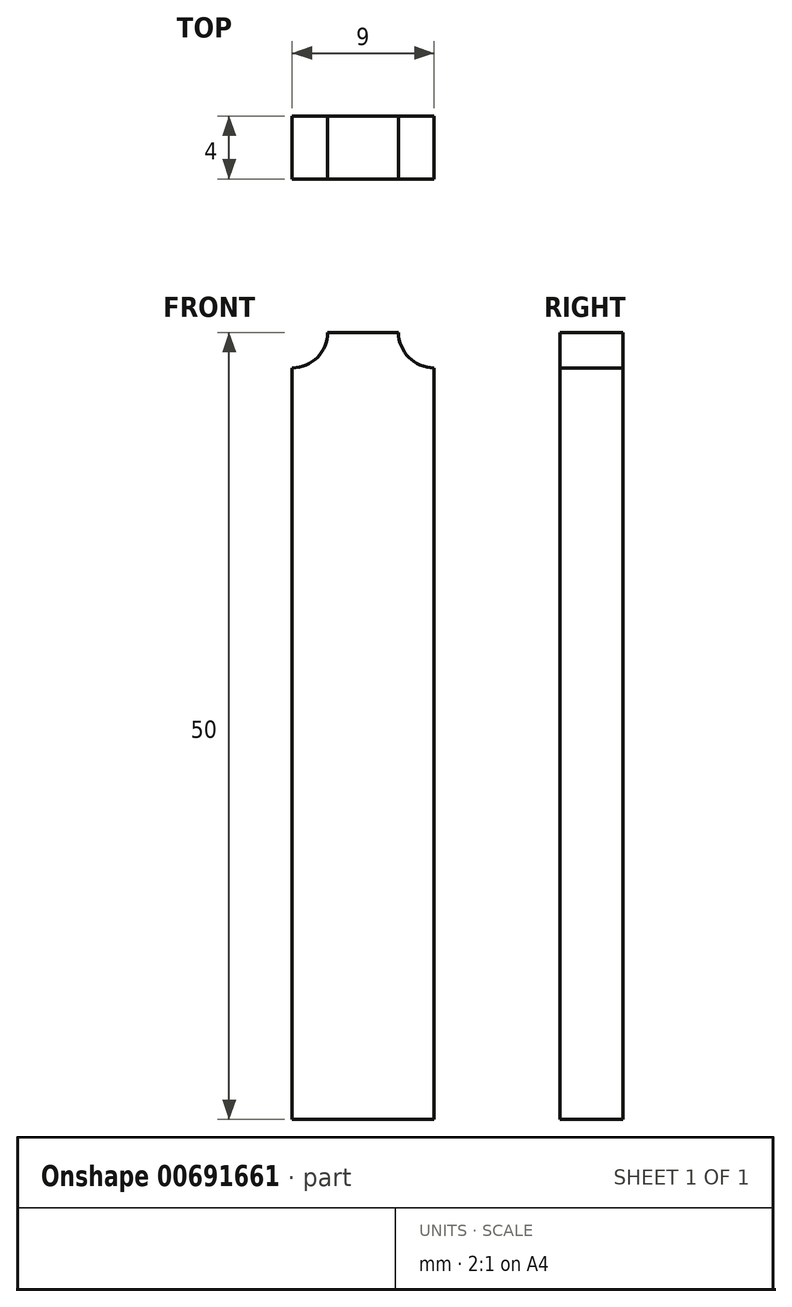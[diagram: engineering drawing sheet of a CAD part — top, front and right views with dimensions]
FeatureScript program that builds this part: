
annotation { "Feature Type Name" : "Feature", "Feature Type Description" : "" }
export const myFeature = defineFeature(function(context is Context, id is Id, definition is map)
    precondition{}
    {
        {
            var Q0;
            Q0=qCreatedBy(makeId("Front.planeOp"),FACE);
            var sketch = newSketch(context, id + "F0", { "sketchPlane" : qUnion([Q0])});
            skLineSegment(sketch, "E0.bottom", {"start": v(-4.5, 0) * mm, "end": v(4.5, 0) * mm});
            skLineSegment(sketch, "E0.top", {"start": v(-4.5, -50) * mm, "end": v(4.5, -50) * mm});
            skLineSegment(sketch, "E0.left", {"start": v(-4.5, 0) * mm, "end": v(-4.5, -50) * mm});
            skLineSegment(sketch, "E0.right", {"start": v(4.5, 0) * mm, "end": v(4.5, -50) * mm});
            skLineSegment(sketch, "E1.bottom", {"start": v(-2.25, 29.05) * mm, "end": v(2.25, 29.05) * mm});
            skLineSegment(sketch, "E1.top", {"start": v(-2.25, 0) * mm, "end": v(2.25, 0) * mm});
            skLineSegment(sketch, "E1.left", {"start": v(-2.25, 29.05) * mm, "end": v(-2.25, 0) * mm});
            skLineSegment(sketch, "E1.right", {"start": v(2.25, 29.05) * mm, "end": v(2.25, 0) * mm});
            skLineSegment(sketch, "E2", {"start": v(0, 22) * mm, "end": v(0, 13) * mm});
            skLineSegment(sketch, "E3.bottom", {"start": v(33.74, -3.72) * mm, "end": v(46.18, -3.72) * mm});
            skLineSegment(sketch, "E3.top", {"start": v(33.74, -42.5) * mm, "end": v(46.18, -42.5) * mm});
            skLineSegment(sketch, "E3.left", {"start": v(33.74, -3.72) * mm, "end": v(33.74, -42.5) * mm});
            skLineSegment(sketch, "E3.right", {"start": v(46.18, -3.72) * mm, "end": v(46.18, -42.5) * mm});
            skLineSegment(sketch, "E4", {"start": v(46.18, -8.55) * mm, "end": v(42.11, -6.2) * mm});
            skLineSegment(sketch, "E5", {"start": v(42.11, -6.2) * mm, "end": v(42.11, -13.68) * mm});
            skLineSegment(sketch, "E6", {"start": v(42.11, -13.68) * mm, "end": v(46.18, -11.33) * mm});
            skLineSegment(sketch, "E7.0.1.0", {"start": v(46.18, -20.55) * mm, "end": v(42.11, -18.2) * mm});
            skLineSegment(sketch, "E7.0.1.1", {"start": v(42.11, -18.2) * mm, "end": v(42.11, -25.68) * mm});
            skLineSegment(sketch, "E7.0.1.2", {"start": v(42.11, -25.68) * mm, "end": v(46.18, -23.33) * mm});
            skLineSegment(sketch, "E7.0.2.0", {"start": v(46.18, -32.55) * mm, "end": v(42.11, -30.2) * mm});
            skLineSegment(sketch, "E7.0.2.1", {"start": v(42.11, -30.2) * mm, "end": v(42.11, -37.68) * mm});
            skLineSegment(sketch, "E7.0.2.2", {"start": v(42.11, -37.68) * mm, "end": v(46.18, -35.33) * mm});
            skLineSegment(sketch, "E7.direction1", {"start": v(42.11, -13.68) * mm, "end": v(67.11, -13.68) * mm, "construction": true});
            skLineSegment(sketch, "E7.direction2", {"start": v(42.11, -13.68) * mm, "end": v(42.11, -25.68) * mm, "construction": true});
            skLineSegment(sketch, "E8.0", {"start": v(41.91, -14.03) * mm, "end": v(46.18, -11.57) * mm});
            skLineSegment(sketch, "E8.1", {"start": v(41.91, -5.86) * mm, "end": v(41.91, -14.03) * mm});
            skLineSegment(sketch, "E8.2", {"start": v(46.18, -8.32) * mm, "end": v(41.91, -5.86) * mm});
            skArc(sketch, "E9.0.startCap", {"start": v(-1, 22) * mm, "mid": v(0, 23) * mm, "end": v(1, 22) * mm});
            skArc(sketch, "E9.0.endCap", {"start": v(1, 13) * mm, "mid": v(0, 12) * mm, "end": v(-1, 13) * mm});
            skLineSegment(sketch, "E9.0.left", {"start": v(1, 22) * mm, "end": v(1, 13) * mm});
            skLineSegment(sketch, "E9.0.right", {"start": v(-1, 22) * mm, "end": v(-1, 13) * mm});
            skFitSpline(sketch, "E10", {"points": [v(0, 29.05) * mm, v(-1.01, 28.43) * mm, v(-1.8, 25.53) * mm, v(-2.25, 21.02) * mm], "startDerivative": vector(-5.04, -1.79) * mm, "endDerivative": vector(-0.93, -10.66) * mm});
            skFitSpline(sketch, "E11.MirrorCS", {"points": [v(0, 29.05) * mm, v(1.01, 28.43) * mm, v(1.8, 25.53) * mm, v(2.25, 21.02) * mm], "startDerivative": vector(5.04, -1.79) * mm, "endDerivative": vector(0.93, -10.66) * mm});
            skSolve(sketch);
        }
        {
            var Q0;
            {var subQ1=sQuery(id+"F0.wireOp",EDGE,"E1.top");Q0=makeQuery(id+"F0.imprint","IMPRINT",FACE,{"disambiguationData":[TD([[makeQuery(id+"F0.imprint","IMPRINT",EDGE,{"derivedFrom":subQ1}),1.0]])]});}
            var Q1;
            Q1=makeQuery(id+"F0.imprint","IMPRINT",FACE,{"disambiguationData":[TD([[makeQuery(id+"F0.imprint","IMPRINT",EDGE,{"derivedFrom":sQuery(id+"F0.wireOp",EDGE,"E0.top")}),1.0]])]});
            extrude(context, id + "F1", {"entities" : qUnion([Q0, Q1]), "depth" : 4 * mm, "offsetDistance" : 25 * mm});
        }
        {
            var Q0;
            Q0=makeQuery(id+"F1.opExtrude","CAP_FACE",FACE,{"disambiguationData":[OSD([sQuery(id+"F0.wireOp",EDGE,"E0.bottom"),sQuery(id+"F0.wireOp",EDGE,"E0.top"),sQuery(id+"F0.wireOp",EDGE,"E0.left"),sQuery(id+"F0.wireOp",EDGE,"E0.right"),sQuery(id+"F0.wireOp",EDGE,"E1.left"),sQuery(id+"F0.wireOp",EDGE,"E1.right"),sQuery(id+"F0.wireOp",EDGE,"E9.0.startCap"),sQuery(id+"F0.wireOp",EDGE,"E9.0.endCap"),sQuery(id+"F0.wireOp",EDGE,"E9.0.left"),sQuery(id+"F0.wireOp",EDGE,"E9.0.right"),sQuery(id+"F0.wireOp",EDGE,"E10"),sQuery(id+"F0.wireOp",EDGE,"E11.MirrorCS")])],"isStart":false});
            var sketch = newSketch(context, id + "F2", { "sketchPlane" : qUnion([Q0])});
            skCircle(sketch, "E12", {"center": v(4.5, 0) * mm, "radius": 2.25 * mm});
            skCircle(sketch, "E13", {"center": v(-4.5, 0) * mm, "radius": 2.25 * mm});
            skSolve(sketch);
        }
        {
            var Q0;
            {var subQ2=sQuery(id+"F0.wireOp",EDGE,"E0.right");var subQ3=sQuery(id+"F0.wireOp",EDGE,"E0.bottom");var subQ4=makeQuery(id+"F1.opExtrude","CAP_EDGE",EDGE,{"disambiguationData":[OSD([subQ3]),TDD([makeQuery(id+"F0.imprint","IMPRINT",EDGE,{"disambiguationData":[TD([[makeQuery(id+"F0.imprint","INTERSECT",VERTEX,{"derivedFrom":[subQ3,subQ2]}),1.0]])],"derivedFrom":subQ3})])],"isStart":false});Q0=makeQuery(id+"F2.imprint","IMPRINT",FACE,{"disambiguationData":[TD([[makeQuery(id+"F2.imprint","IMPRINT",EDGE,{"derivedFrom":subQ4}),-1.0]])]});}
            var Q1;
            {var subQ2=sQuery(id+"F0.wireOp",EDGE,"E0.left");var subQ3=sQuery(id+"F0.wireOp",EDGE,"E0.bottom");var subQ4=makeQuery(id+"F1.opExtrude","CAP_EDGE",EDGE,{"disambiguationData":[OSD([subQ3]),TDD([makeQuery(id+"F0.imprint","IMPRINT",EDGE,{"disambiguationData":[TD([[makeQuery(id+"F0.imprint","INTERSECT",VERTEX,{"derivedFrom":[subQ3,subQ2]}),-1.0]])],"derivedFrom":subQ3})])],"isStart":false});Q1=makeQuery(id+"F2.imprint","IMPRINT",FACE,{"disambiguationData":[TD([[makeQuery(id+"F2.imprint","IMPRINT",EDGE,{"derivedFrom":subQ4}),-1.0]])]});}
            extrude(context, id + "F3", {"entities" : qUnion([Q0, Q1]), "operationType" : NewBodyOperationType.REMOVE, "endBound" : BoundingType.THROUGH_ALL, "oppositeDirection" : true, "depth" : 25 * mm, "offsetDistance" : 25 * mm});
        }
    });
